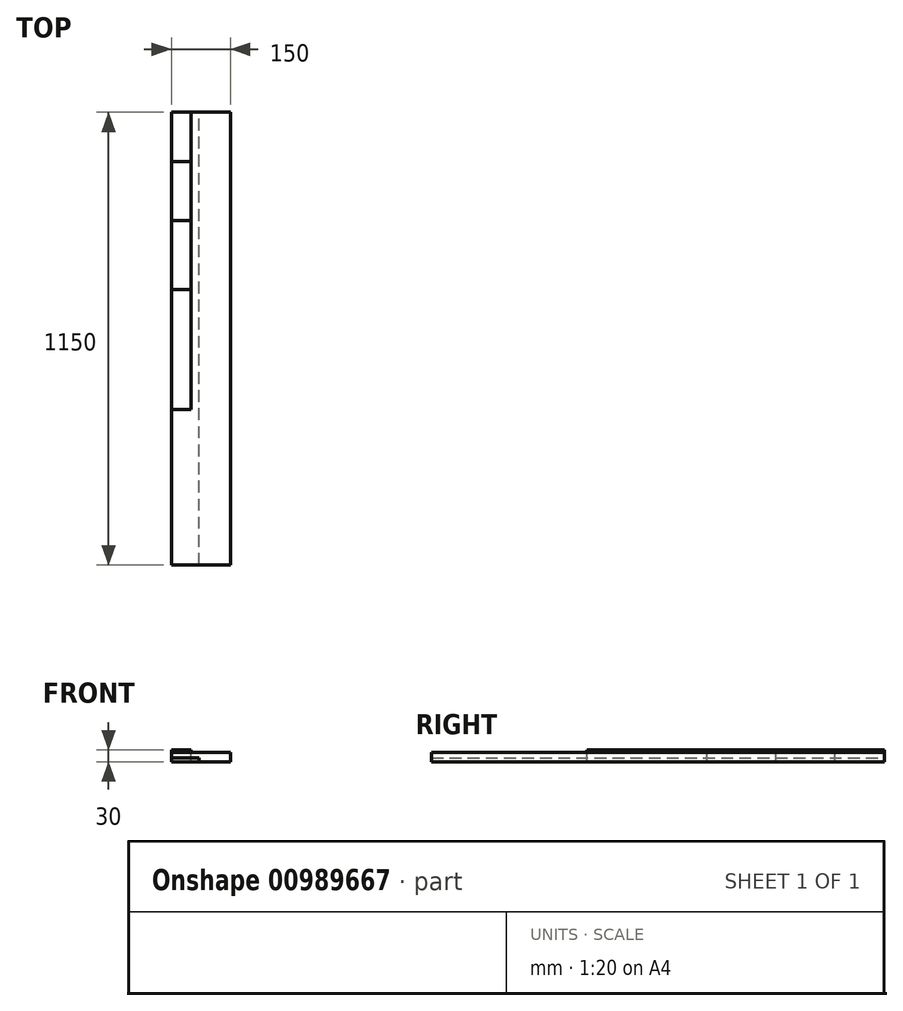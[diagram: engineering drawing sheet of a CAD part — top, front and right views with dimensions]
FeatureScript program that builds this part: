
annotation { "Feature Type Name" : "Feature", "Feature Type Description" : "" }
export const myFeature = defineFeature(function(context is Context, id is Id, definition is map)
    precondition{}
    {
        {
            var Q0;
            Q0=qCreatedBy(makeId("Front.planeOp"),FACE);
            var sketch = newSketch(context, id + "F0", { "sketchPlane" : qUnion([Q0])});
            skLineSegment(sketch, "E0.bottom", {"start": v(0, 0) * mm, "end": v(150, 0) * mm});
            skLineSegment(sketch, "E0.top", {"start": v(0, 24) * mm, "end": v(150, 24) * mm});
            skLineSegment(sketch, "E0.left", {"start": v(0, 0) * mm, "end": v(0, 24) * mm});
            skLineSegment(sketch, "E0.right", {"start": v(150, 0) * mm, "end": v(150, 24) * mm});
            skSolve(sketch);
        }
        {
            var Q0;
            Q0=makeQuery(id+"F0.imprint","IMPRINT",FACE,{"disambiguationData":[TD([[makeQuery(id+"F0.imprint","IMPRINT",EDGE,{"derivedFrom":sQuery(id+"F0.wireOp",EDGE,"E0.bottom")}),1.0]])]});
            extrude(context, id + "F1", {"entities" : qUnion([Q0]), "depth" : 1150 * mm, "offsetDistance" : 25 * mm});
        }
        {
            var Q0;
            Q0=qCreatedBy(makeId("Front.planeOp"),FACE);
            var sketch = newSketch(context, id + "F2", { "sketchPlane" : qUnion([Q0])});
            skLineSegment(sketch, "E1.bottom", {"start": v(0, 0) * mm, "end": v(70, 0) * mm});
            skLineSegment(sketch, "E1.top", {"start": v(0, 10) * mm, "end": v(70, 10) * mm});
            skLineSegment(sketch, "E1.left", {"start": v(0, 0) * mm, "end": v(0, 10) * mm});
            skLineSegment(sketch, "E1.right", {"start": v(70, 0) * mm, "end": v(70, 10) * mm});
            skSolve(sketch);
        }
        {
            var Q0;
            Q0=qCreatedBy(makeId("Front.planeOp"),FACE);
            var sketch = newSketch(context, id + "F3", { "sketchPlane" : qUnion([Q0])});
            skLineSegment(sketch, "E2.bottom", {"start": v(0, 0) * mm, "end": v(50, 0) * mm});
            skLineSegment(sketch, "E2.top", {"start": v(0, 30) * mm, "end": v(50, 30) * mm});
            skLineSegment(sketch, "E2.left", {"start": v(0, 0) * mm, "end": v(0, 30) * mm});
            skLineSegment(sketch, "E2.right", {"start": v(50, 0) * mm, "end": v(50, 30) * mm});
            skSolve(sketch);
        }
        {
            var Q0;
            Q0 = qSketchRegion(id + "F3", true);
            extrude(context, id + "F4", {"entities" : qUnion([Q0]), "depth" : 450 * mm, "offsetDistance" : 25 * mm});
        }
        {
            var Q0;
            Q0 = qSketchRegion(id + "F3", true);
            extrude(context, id + "F5", {"entities" : qUnion([Q0]), "depth" : 755 * mm, "offsetDistance" : 25 * mm});
        }
        {
            var Q0;
            Q0 = qSketchRegion(id + "F3", true);
            extrude(context, id + "F6", {"entities" : qUnion([Q0]), "depth" : 275 * mm, "offsetDistance" : 25 * mm});
        }
        {
            var Q0;
            Q0 = qSketchRegion(id + "F3", true);
            extrude(context, id + "F7", {"entities" : qUnion([Q0]), "depth" : 125 * mm, "offsetDistance" : 25 * mm});
        }
        {
            var Q0;
            Q0 = qSketchRegion(id + "F2", true);
            extrude(context, id + "F8", {"entities" : qUnion([Q0]), "depth" : 1150 * mm, "offsetDistance" : 25 * mm});
        }
    });
